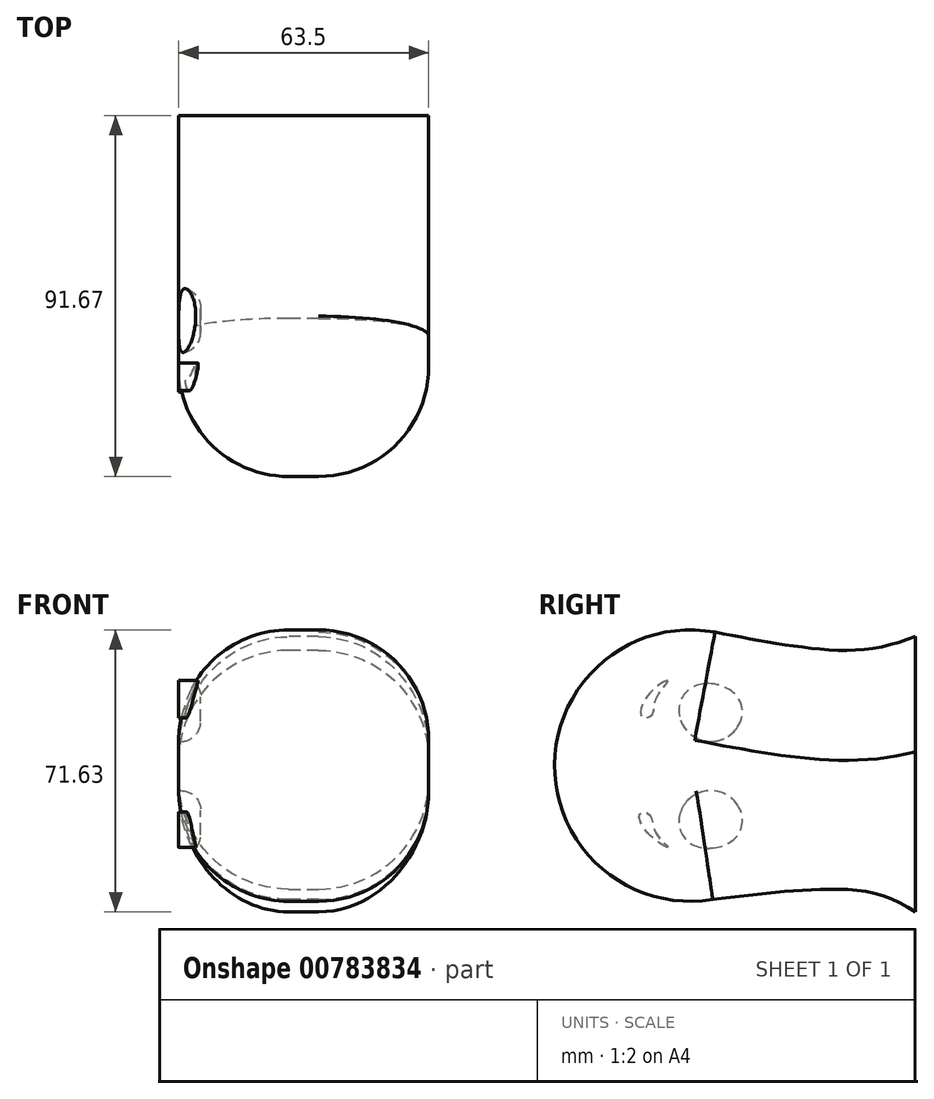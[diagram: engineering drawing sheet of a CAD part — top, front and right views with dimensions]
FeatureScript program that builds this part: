
annotation { "Feature Type Name" : "Feature", "Feature Type Description" : "" }
export const myFeature = defineFeature(function(context is Context, id is Id, definition is map)
    precondition{}
    {
        {
            var Q0;
            Q0=qCreatedBy(makeId("Right.planeOp"),FACE);
            var sketch = newSketch(context, id + "F0", { "sketchPlane" : qUnion([Q0])});
            skFitSpline(sketch, "E0", {"points": [v(0, 32.23) * mm, v(-15.41, 28.8) * mm, v(-50.94, 33.38) * mm], "startDerivative": vector(-34.54, -11.86) * mm, "endDerivative": vector(-65.28, 12.5) * mm});
            skFitSpline(sketch, "E1", {"points": [v(0, -37.68) * mm, v(-12.55, -32.52) * mm, v(-51.52, -34.53) * mm], "startDerivative": vector(-28.62, 17.07) * mm, "endDerivative": vector(-70.79, -8.56) * mm});
            skArc(sketch, "E2", {"start": v(-50.94, 33.38) * mm, "mid": v(-91.67, -0.23) * mm, "end": v(-51.52, -34.53) * mm});
            skLineSegment(sketch, "E3", {"start": v(0, 32.23) * mm, "end": v(0, -37.68) * mm});
            skSolve(sketch);
        }
        {
            var Q0;
            Q0=makeQuery(id+"F0.imprint","IMPRINT",FACE,{"disambiguationData":[TD([[makeQuery(id+"F0.imprint","IMPRINT",EDGE,{"derivedFrom":sQuery(id+"F0.wireOp",EDGE,"E0")}),1.0]])]});
            extrude(context, id + "F1", {"entities" : qUnion([Q0]), "depth" : 63.5 * mm, "offsetDistance" : 25.4 * mm});
        }
        {
            var Q0;
            Q0=makeQuery(id+"F1.opExtrude","CAP_EDGE",EDGE,{"disambiguationData":[OSD([sQuery(id+"F0.wireOp",EDGE,"E0")])],"isStart":false});
            var Q1;
            Q1=makeQuery(id+"F1.opExtrude","CAP_EDGE",EDGE,{"disambiguationData":[OSD([sQuery(id+"F0.wireOp",EDGE,"E0")])],"isStart":true});
            var Q2;
            Q2=makeQuery(id+"F1.opExtrude","CAP_EDGE",EDGE,{"disambiguationData":[OSD([sQuery(id+"F0.wireOp",EDGE,"E1")])],"isStart":false});
            var Q3;
            Q3=makeQuery(id+"F1.opExtrude","CAP_EDGE",EDGE,{"disambiguationData":[OSD([sQuery(id+"F0.wireOp",EDGE,"E2")])],"isStart":false});
            var Q4;
            Q4=makeQuery(id+"F1.opExtrude","CAP_EDGE",EDGE,{"disambiguationData":[OSD([sQuery(id+"F0.wireOp",EDGE,"E2")])],"isStart":true});
            fillet(context, id + "F2", {"entities" : qUnion([Q0, Q1, Q2, Q3, Q4]), "radius" : 27.94 * mm, "tangentPropagation" : true, "allowEdgeOverflow" : false});
        }
        {
            var Q0;
            Q0=qCreatedBy(makeId("Right.planeOp"),FACE);
            var sketch = newSketch(context, id + "F3", { "sketchPlane" : qUnion([Q0])});
            skCircle(sketch, "E4", {"center": v(-52, 13.8) * mm, "radius": 8.18 * mm});
            skCircle(sketch, "E5", {"center": v(-52, -15.04) * mm, "radius": 8.16 * mm});
            skSolve(sketch);
        }
        {
            var Q0;
            Q0 = qSketchRegion(id + "F3", true);
            extrude(context, id + "F4", {"entities" : qUnion([Q0]), "operationType" : NewBodyOperationType.REMOVE, "depth" : 5.6 * mm, "offsetDistance" : 25.4 * mm});
        }
        {
            var Q0;
            Q0=makeQuery(id+"F4.boolean.opBoolean","COPY",EDGE,{"derivedFrom":makeQuery(id+"F4.opExtrude","CAP_EDGE",EDGE,{"disambiguationData":[OSD([sQuery(id+"F3.wireOp",EDGE,"E4")])],"isStart":false})});
            var Q1;
            Q1=makeQuery(id+"F4.boolean.opBoolean","COPY",EDGE,{"derivedFrom":makeQuery(id+"F4.opExtrude","CAP_EDGE",EDGE,{"disambiguationData":[OSD([sQuery(id+"F3.wireOp",EDGE,"E5")])],"isStart":false})});
            fillet(context, id + "F5", {"entities" : qUnion([Q0, Q1]), "radius" : 5.08 * mm, "tangentPropagation" : true, "allowEdgeOverflow" : false});
        }
        {
            var Q0;
            Q0=qCreatedBy(makeId("Right.planeOp"),FACE);
            var sketch = newSketch(context, id + "F6", { "sketchPlane" : qUnion([Q0])});
            skFitSpline(sketch, "E6", {"points": [v(-62.84, 21.03) * mm, v(-67.23, 18.2) * mm, v(-69.55, 12) * mm, v(-66.97, 12.26) * mm, v(-65.94, 16.39) * mm, v(-62.84, 21.03) * mm]});
            skFitSpline(sketch, "E7", {"points": [v(-62.84, -21.3) * mm, v(-66.97, -18.71) * mm, v(-70.07, -12.78) * mm, v(-67.74, -12.78) * mm, v(-65.94, -17.68) * mm, v(-62.84, -21.3) * mm]});
            skSolve(sketch);
        }
        {
            var Q0;
            Q0 = qSketchRegion(id + "F6", true);
            extrude(context, id + "F7", {"entities" : qUnion([Q0]), "operationType" : NewBodyOperationType.ADD, "depth" : 25.4 * mm, "offsetDistance" : 25.4 * mm});
        }
    });
